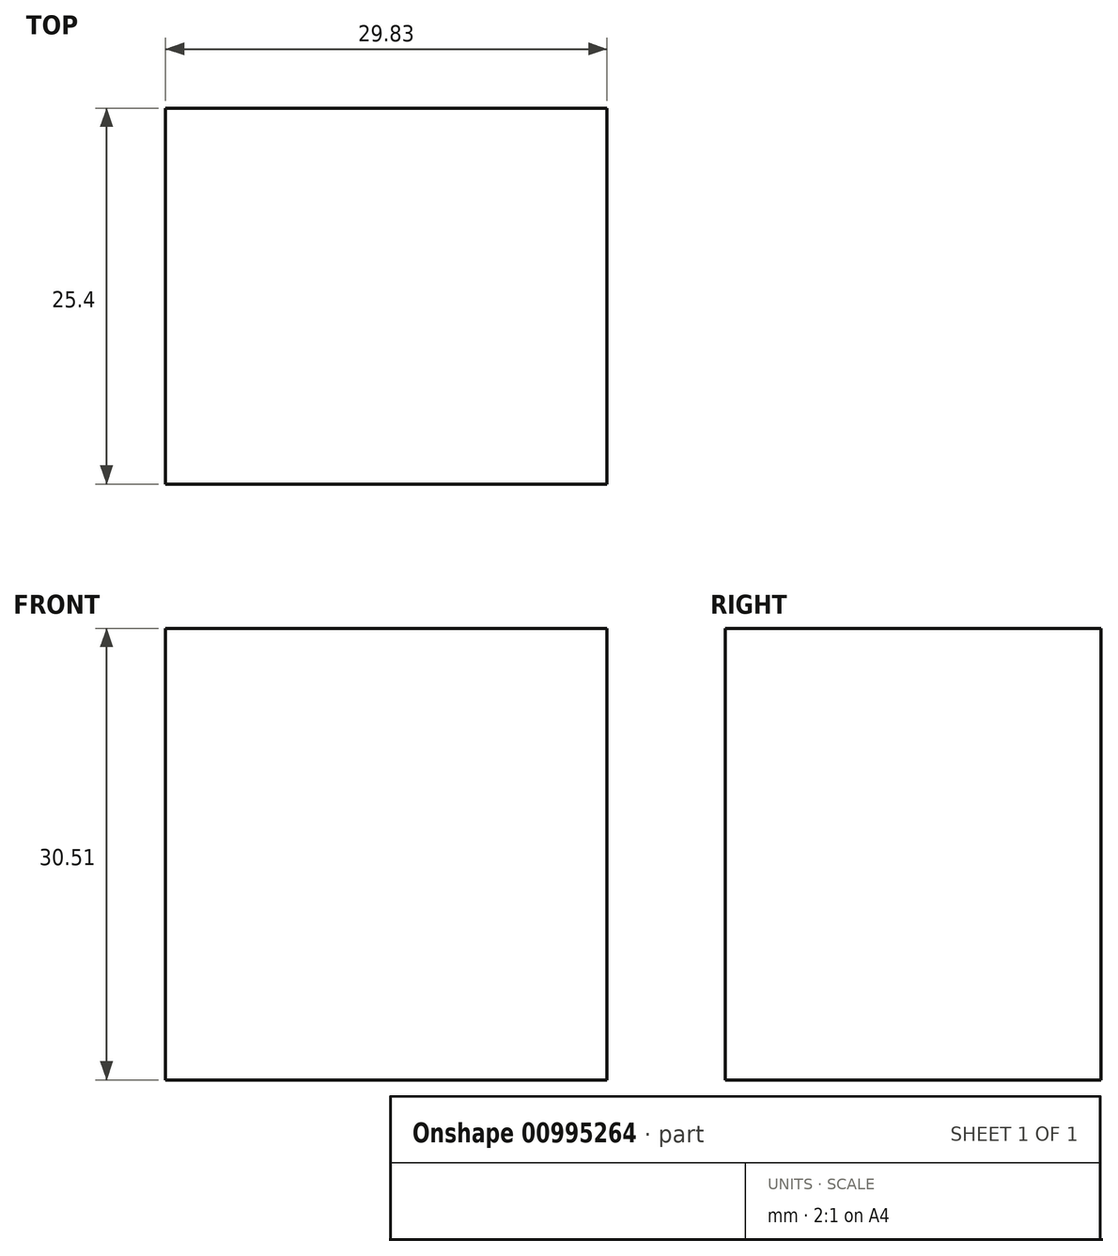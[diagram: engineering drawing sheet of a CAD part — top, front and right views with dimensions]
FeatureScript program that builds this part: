
annotation { "Feature Type Name" : "Feature", "Feature Type Description" : "" }
export const myFeature = defineFeature(function(context is Context, id is Id, definition is map)
    precondition{}
    {
        {
            var Q0;
            Q0=qCreatedBy(makeId("Front.planeOp"),FACE);
            var sketch = newSketch(context, id + "F0", { "sketchPlane" : qUnion([Q0])});
            skLineSegment(sketch, "E0.bottom", {"start": v(0, 0) * mm, "end": v(29.83, 0) * mm});
            skLineSegment(sketch, "E0.top", {"start": v(0, -30.51) * mm, "end": v(29.83, -30.51) * mm});
            skLineSegment(sketch, "E0.left", {"start": v(0, 0) * mm, "end": v(0, -30.51) * mm});
            skLineSegment(sketch, "E0.right", {"start": v(29.83, 0) * mm, "end": v(29.83, -30.51) * mm});
            skSolve(sketch);
        }
        {
            var Q0;
            Q0 = qSketchRegion(id + "F0", true);
            extrude(context, id + "F1", {"entities" : qUnion([Q0]), "depth" : 25.4 * mm, "offsetDistance" : 25.4 * mm});
        }
    });
